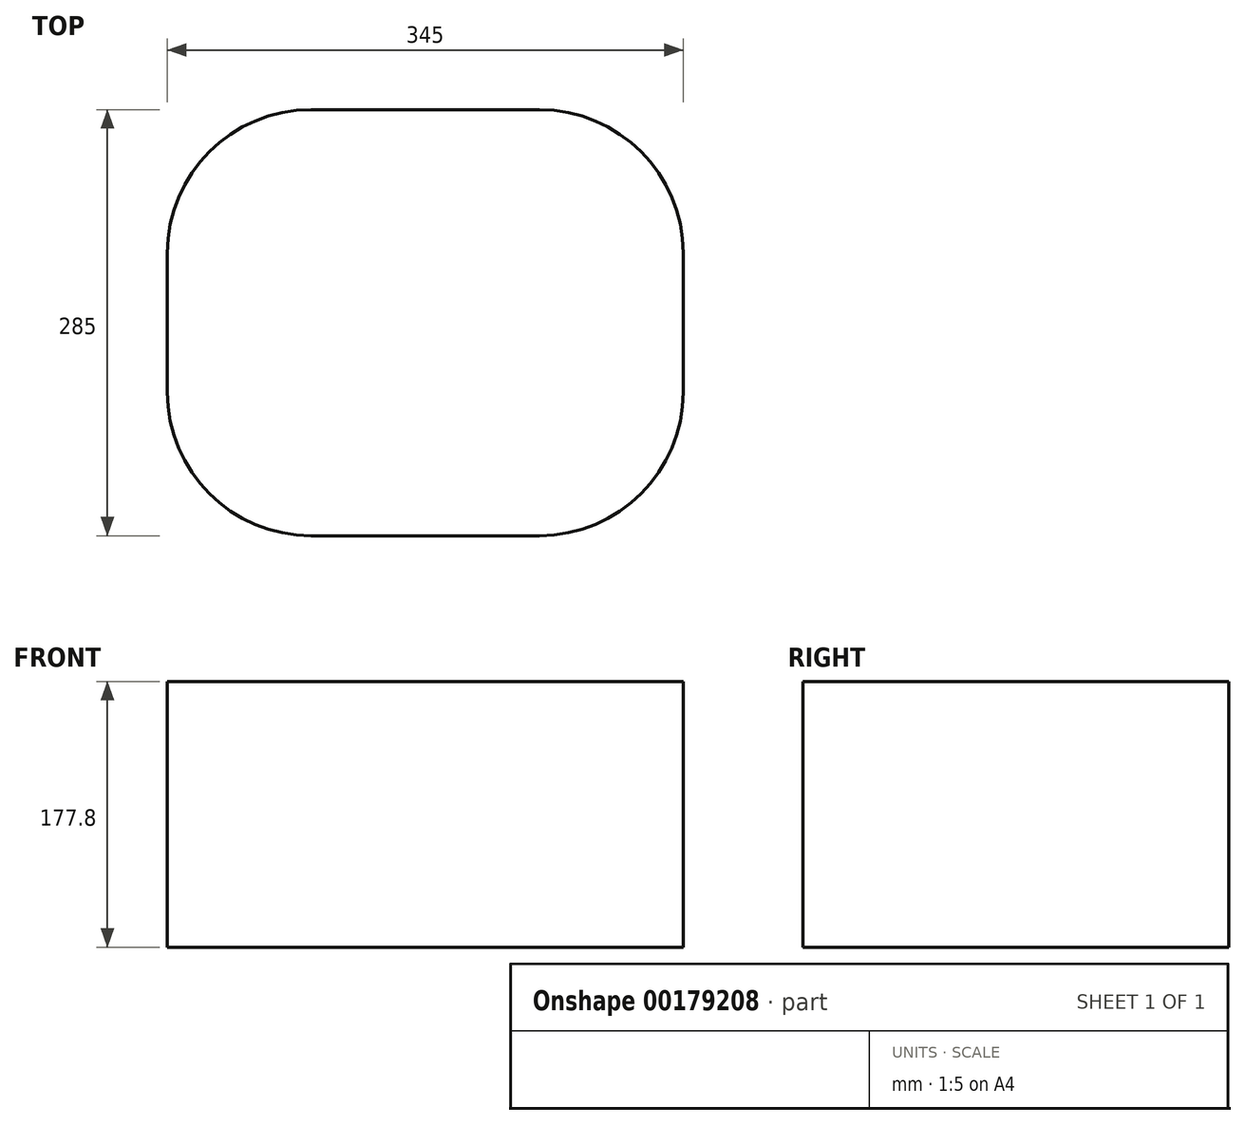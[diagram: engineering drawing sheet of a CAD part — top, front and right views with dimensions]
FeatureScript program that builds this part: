
annotation { "Feature Type Name" : "Feature", "Feature Type Description" : "" }
export const myFeature = defineFeature(function(context is Context, id is Id, definition is map)
    precondition{}
    {
        {
            var Q0;
            Q0=qCreatedBy(makeId("Top.planeOp"),FACE);
            var sketch = newSketch(context, id + "F0", { "sketchPlane" : qUnion([Q0])});
            skLineSegment(sketch, "E0.bottom", {"start": v(-76.5, 142.5) * mm, "end": v(76.5, 142.5) * mm});
            skLineSegment(sketch, "E0.top", {"start": v(-76.5, -142.5) * mm, "end": v(76.5, -142.5) * mm});
            skLineSegment(sketch, "E0.left", {"start": v(-172.5, 46.5) * mm, "end": v(-172.5, -46.5) * mm});
            skLineSegment(sketch, "E0.right", {"start": v(172.5, 46.5) * mm, "end": v(172.5, -46.5) * mm});
            skLineSegment(sketch, "E1", {"start": v(0, 142.5) * mm, "end": v(0, -142.5) * mm, "construction": true});
            skPoint(sketch, "E2.visualSharp", {"position": v(-172.5, 142.5) * mm});
            skArc(sketch, "E2.filletArc", {"start": v(-76.5, 142.5) * mm, "mid": v(-144.38, 114.38) * mm, "end": v(-172.5, 46.5) * mm});
            skPoint(sketch, "E3.visualSharp", {"position": v(172.5, 142.5) * mm});
            skArc(sketch, "E3.filletArc", {"start": v(172.5, 46.5) * mm, "mid": v(144.38, 114.38) * mm, "end": v(76.5, 142.5) * mm});
            skPoint(sketch, "E4.visualSharp", {"position": v(172.5, -142.5) * mm});
            skArc(sketch, "E4.filletArc", {"start": v(76.5, -142.5) * mm, "mid": v(144.38, -114.38) * mm, "end": v(172.5, -46.5) * mm});
            skPoint(sketch, "E5.visualSharp", {"position": v(-172.5, -142.5) * mm});
            skArc(sketch, "E5.filletArc", {"start": v(-172.5, -46.5) * mm, "mid": v(-144.38, -114.38) * mm, "end": v(-76.5, -142.5) * mm});
            skSolve(sketch);
        }
        {
            var Q0;
            Q0=makeQuery(id+"F0.imprint","IMPRINT",FACE,{"disambiguationData":[TD([[makeQuery(id+"F0.imprint","IMPRINT",EDGE,{"derivedFrom":sQuery(id+"F0.wireOp",EDGE,"E0.bottom")}),-1.0]])]});
            extrude(context, id + "F1", {"entities" : qUnion([Q0]), "oppositeDirection" : true, "depth" : 177.8 * mm});
        }
    });
